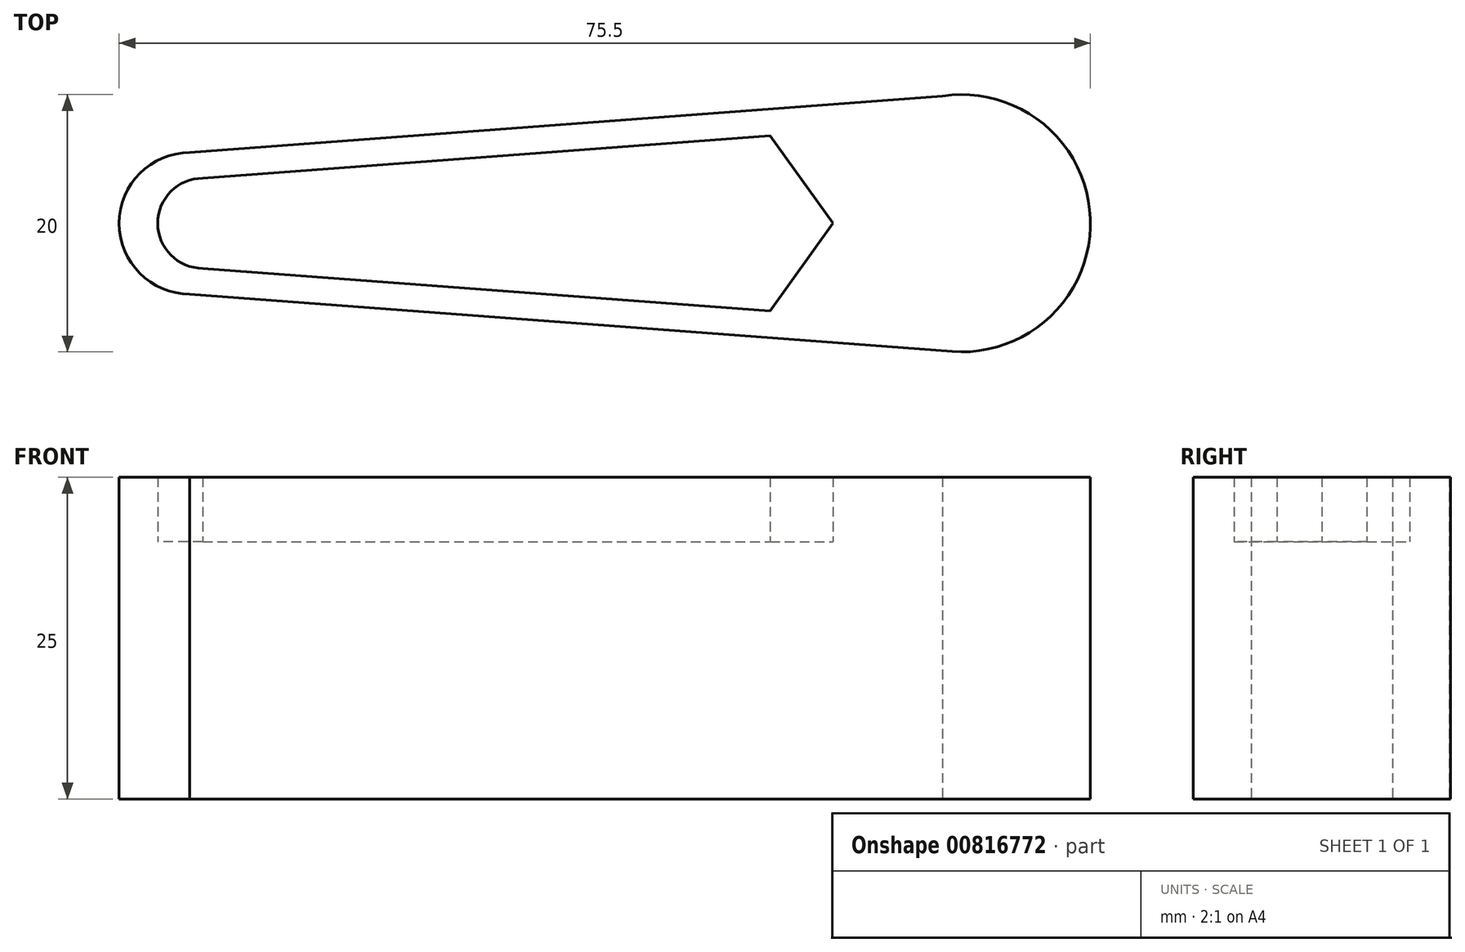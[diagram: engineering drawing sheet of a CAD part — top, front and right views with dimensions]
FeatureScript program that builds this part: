
annotation { "Feature Type Name" : "Feature", "Feature Type Description" : "" }
export const myFeature = defineFeature(function(context is Context, id is Id, definition is map)
    precondition{}
    {
        {
            var Q0;
            Q0=qCreatedBy(makeId("Top.planeOp"),FACE);
            var sketch = newSketch(context, id + "F0", { "sketchPlane" : qUnion([Q0])});
            skCircle(sketch, "E0", {"center": v(0, 0) * mm, "radius": 10 * mm});
            skCircle(sketch, "E1", {"center": v(0, 0) * mm, "radius": 7 * mm});
            skCircle(sketch, "E2", {"center": v(0, 0) * mm, "radius": 6 * mm});
            skArc(sketch, "E3", {"start": v(-60, 5.5) * mm, "mid": v(-65.5, 0) * mm, "end": v(-60, -5.5) * mm});
            skLineSegment(sketch, "E4", {"start": v(-60, 5.5) * mm, "end": v(0, 10) * mm});
            skLineSegment(sketch, "E5", {"start": v(-60, -5.5) * mm, "end": v(0, -10.03) * mm});
            skArc(sketch, "E6", {"start": v(-59.85, 3.5) * mm, "mid": v(-63.5, 0) * mm, "end": v(-59.85, -3.5) * mm});
            skLineSegment(sketch, "E7", {"start": v(-60, 5.5) * mm, "end": v(-59.85, 3.5) * mm});
            skLineSegment(sketch, "E8", {"start": v(-60, -5.5) * mm, "end": v(-59.85, -3.5) * mm});
            skPoint(sketch, "E9.orphan", {"position": v(-30, -7.76) * mm});
            skPoint(sketch, "E10.orphan", {"position": v(-30, 7.75) * mm});
            skLineSegment(sketch, "E11", {"start": v(-59.85, -3.5) * mm, "end": v(-6.6, -7.52) * mm});
            skLineSegment(sketch, "E12", {"start": v(-59.85, 3.5) * mm, "end": v(-6.63, 7.49) * mm});
            skLineSegment(sketch, "E13", {"start": v(-10, 0) * mm, "end": v(-23.58, -6.23) * mm});
            skLineSegment(sketch, "E14", {"start": v(-23.58, 6.22) * mm, "end": v(-10, 0) * mm});
            skSolve(sketch);
        }
        {
            var Q0;
            Q0 = qSketchRegion(id + "F0", true);
            var Q1;
            {var subQ3=sQuery(id+"F0.wireOp",EDGE,"E13");Q1=makeQuery(id+"F0.imprint","IMPRINT",FACE,{"disambiguationData":[TD([[makeQuery(id+"F0.imprint","IMPRINT",EDGE,{"derivedFrom":subQ3}),1.0]])]});}
            var Q2;
            {var subQ3=sQuery(id+"F0.wireOp",EDGE,"E14");Q2=makeQuery(id+"F0.imprint","IMPRINT",FACE,{"disambiguationData":[TD([[makeQuery(id+"F0.imprint","IMPRINT",EDGE,{"derivedFrom":subQ3}),1.0]])]});}
            var Q3;
            {var subQ2=sQuery(id+"F0.wireOp",EDGE,"E6");Q3=makeQuery(id+"F0.imprint","IMPRINT",FACE,{"disambiguationData":[TD([[makeQuery(id+"F0.imprint","IMPRINT",EDGE,{"derivedFrom":subQ2}),1.0]])]});}
            var Q4;
            Q4=makeQuery(id+"F0.imprint","IMPRINT",FACE,{"disambiguationData":[TD([[makeQuery(id+"F0.imprint","IMPRINT",EDGE,{"derivedFrom":sQuery(id+"F0.wireOp",EDGE,"E2")}),1.0]])]});
            var Q5;
            Q5=makeQuery(id+"F0.imprint","IMPRINT",FACE,{"disambiguationData":[TD([[makeQuery(id+"F0.imprint","IMPRINT",EDGE,{"derivedFrom":sQuery(id+"F0.wireOp",EDGE,"E1")}),1.0]])]});
            extrude(context, id + "F1", {"entities" : qUnion([Q0, Q1, Q2, Q3, Q4, Q5]), "depth" : 25 * mm, "offsetDistance" : 25 * mm});
        }
        {
            var Q0;
            Q0=qCreatedBy(makeId("Top.planeOp"),FACE);
            var sketch = newSketch(context, id + "F2", { "sketchPlane" : qUnion([Q0])});
            skCircle(sketch, "E15", {"center": v(-59, 0) * mm, "radius": 3.5 * mm});
            skArc(sketch, "E16.0.0", {"start": v(-0.75, -9.97) * mm, "mid": v(10, 0.37) * mm, "end": v(-1.5, 9.89) * mm});
            skLineSegment(sketch, "E16.0.1", {"start": v(-1.5, 9.89) * mm, "end": v(-60, 5.5) * mm});
            skArc(sketch, "E16.0.2", {"start": v(-60, 5.5) * mm, "mid": v(-65.5, 0) * mm, "end": v(-60, -5.5) * mm});
            skLineSegment(sketch, "E16.0.3", {"start": v(-60, -5.5) * mm, "end": v(-0.75, -9.97) * mm});
            skLineSegment(sketch, "E17", {"start": v(-59, -3.5) * mm, "end": v(-14.9, -6.83) * mm});
            skLineSegment(sketch, "E18", {"start": v(-59, 3.5) * mm, "end": v(-14.9, 6.8) * mm});
            skLineSegment(sketch, "E19", {"start": v(-14.9, -6.83) * mm, "end": v(-10, 0) * mm});
            skLineSegment(sketch, "E20", {"start": v(-10, 0) * mm, "end": v(-14.9, 6.8) * mm});
            skSolve(sketch);
        }
        {
            var Q0;
            {var subQ1=sQuery(id+"F2.wireOp",EDGE,"E17");Q0=makeQuery(id+"F2.imprint","IMPRINT",FACE,{"disambiguationData":[TD([[makeQuery(id+"F2.imprint","IMPRINT",EDGE,{"derivedFrom":subQ1}),1.0]])]});}
            var Q1;
            {var subQ0=sQuery(id+"F2.wireOp",EDGE,"E15");var subQ1=makeQuery(id+"F2.imprint","INTERSECT",VERTEX,{"derivedFrom":[subQ0,sQuery(id+"F2.wireOp",EDGE,"E17")]});Q1=makeQuery(id+"F2.imprint","IMPRINT",FACE,{"disambiguationData":[TD([[makeQuery(id+"F2.imprint","IMPRINT",EDGE,{"disambiguationData":[TD([[subQ1,1.0]])],"derivedFrom":subQ0}),1.0]])]});}
            extrude(context, id + "F3", {"entities" : qUnion([Q0, Q1]), "operationType" : NewBodyOperationType.REMOVE, "depth" : 30 * mm, "offsetDistance" : 25 * mm, "hasSecondDirection" : true, "secondDirectionOppositeDirection" : false, "secondDirectionDepth" : 20 * mm});
        }
    });
